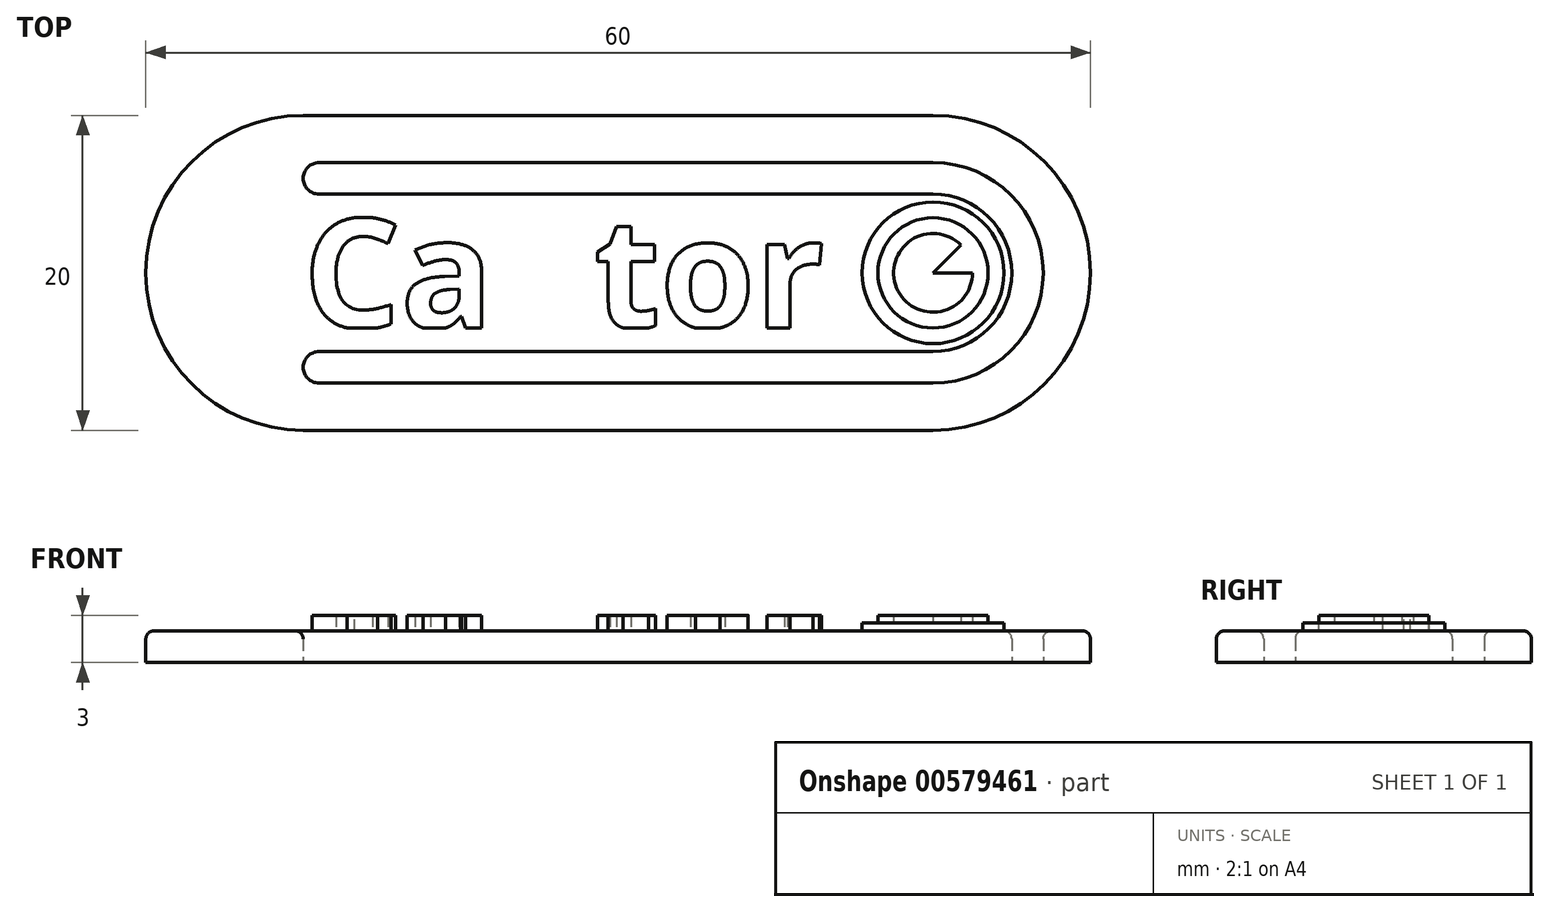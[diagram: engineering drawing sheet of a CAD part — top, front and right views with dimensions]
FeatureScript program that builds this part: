
annotation { "Feature Type Name" : "Feature", "Feature Type Description" : "" }
export const myFeature = defineFeature(function(context is Context, id is Id, definition is map)
    precondition{}
    {
        {
            var Q0;
            Q0=qCreatedBy(makeId("Top.planeOp"),FACE);
            var sketch = newSketch(context, id + "F0", { "sketchPlane" : qUnion([Q0])});
            skLineSegment(sketch, "E0.bottom", {"start": v(10, 0) * mm, "end": v(50, 0) * mm});
            skLineSegment(sketch, "E0.top", {"start": v(10, 20) * mm, "end": v(50, 20) * mm});
            skLineSegment(sketch, "E0.left", {"start": v(0, 10) * mm, "end": v(0, 10) * mm});
            skLineSegment(sketch, "E0.right", {"start": v(60, 10) * mm, "end": v(60, 10) * mm});
            skPoint(sketch, "E1.visualSharp", {"position": v(0, 0) * mm});
            skArc(sketch, "E1.filletArc", {"start": v(0, 10) * mm, "mid": v(2.93, 2.93) * mm, "end": v(10, 0) * mm});
            skPoint(sketch, "E2.visualSharp", {"position": v(0, 20) * mm});
            skArc(sketch, "E2.filletArc", {"start": v(10, 20) * mm, "mid": v(2.93, 17.07) * mm, "end": v(0, 10) * mm});
            skPoint(sketch, "E3.visualSharp", {"position": v(60, 20) * mm});
            skArc(sketch, "E3.filletArc", {"start": v(60, 10) * mm, "mid": v(57.07, 17.07) * mm, "end": v(50, 20) * mm});
            skPoint(sketch, "E4.visualSharp", {"position": v(60, 0) * mm});
            skArc(sketch, "E4.filletArc", {"start": v(50, 0) * mm, "mid": v(57.07, 2.93) * mm, "end": v(60, 10) * mm});
            skLineSegment(sketch, "E5.0", {"start": v(11, 3) * mm, "end": v(50, 3) * mm});
            skArc(sketch, "E5.1", {"start": v(50, 3) * mm, "mid": v(54.95, 5.05) * mm, "end": v(57, 10) * mm});
            skArc(sketch, "E5.2", {"start": v(57, 10) * mm, "mid": v(54.95, 14.95) * mm, "end": v(50, 17) * mm});
            skLineSegment(sketch, "E5.3", {"start": v(11, 17) * mm, "end": v(50, 17) * mm});
            skLineSegment(sketch, "E6.0", {"start": v(11, 5) * mm, "end": v(50, 5) * mm});
            skArc(sketch, "E6.1", {"start": v(50, 5) * mm, "mid": v(53.54, 6.46) * mm, "end": v(55, 10) * mm});
            skArc(sketch, "E6.2", {"start": v(55, 10) * mm, "mid": v(53.54, 13.54) * mm, "end": v(50, 15) * mm});
            skLineSegment(sketch, "E6.3", {"start": v(11, 15) * mm, "end": v(50, 15) * mm});
            skLineSegment(sketch, "E7", {"start": v(10, 16) * mm, "end": v(10, 16) * mm});
            skLineSegment(sketch, "E8", {"start": v(10, 4) * mm, "end": v(10, 4) * mm});
            skLineSegment(sketch, "E9.bottom", {"start": v(-20.23, 39.05) * mm, "end": v(-8.15, 39.05) * mm});
            skLineSegment(sketch, "E9.top", {"start": v(-21.23, 29.78) * mm, "end": v(-8.15, 29.78) * mm});
            skLineSegment(sketch, "E9.left", {"start": v(-21.23, 38.05) * mm, "end": v(-21.23, 29.78) * mm});
            skLineSegment(sketch, "E9.right", {"start": v(-8.15, 39.05) * mm, "end": v(-8.15, 29.78) * mm});
            skPoint(sketch, "E10.visualSharp", {"position": v(-21.23, 39.05) * mm});
            skArc(sketch, "E10.filletArc", {"start": v(-20.23, 39.05) * mm, "mid": v(-20.94, 38.76) * mm, "end": v(-21.23, 38.05) * mm});
            skPoint(sketch, "E11.visualSharp", {"position": v(10, 3) * mm});
            skArc(sketch, "E11.filletArc", {"start": v(10, 4) * mm, "mid": v(10.3, 3.3) * mm, "end": v(11, 3) * mm});
            skPoint(sketch, "E12.visualSharp", {"position": v(10, 5) * mm});
            skArc(sketch, "E12.filletArc", {"start": v(11, 5) * mm, "mid": v(10.3, 4.7) * mm, "end": v(10, 4) * mm});
            skPoint(sketch, "E13.visualSharp", {"position": v(10, 15) * mm});
            skArc(sketch, "E13.filletArc", {"start": v(10, 16) * mm, "mid": v(10.3, 15.3) * mm, "end": v(11, 15) * mm});
            skPoint(sketch, "E14.visualSharp", {"position": v(10, 17) * mm});
            skArc(sketch, "E14.filletArc", {"start": v(11, 17) * mm, "mid": v(10.3, 16.7) * mm, "end": v(10, 16) * mm});
            skSolve(sketch);
        }
        {
            var Q0;
            Q0=makeQuery(id+"F0.imprint","IMPRINT",FACE,{"disambiguationData":[TD([[makeQuery(id+"F0.imprint","IMPRINT",EDGE,{"derivedFrom":sQuery(id+"F0.wireOp",EDGE,"E0.bottom")}),1.0]])]});
            extrude(context, id + "F1", {"entities" : qUnion([Q0]), "depth" : 2 * mm, "offsetDistance" : 25 * mm});
        }
        {
            var Q0;
            Q0=makeQuery(id+"F1.opExtrude","CAP_EDGE",EDGE,{"disambiguationData":[OSD([sQuery(id+"F0.wireOp",EDGE,"E1.filletArc"),sQuery(id+"F0.wireOp",EDGE,"E2.filletArc")])],"isStart":false});
            var Q1;
            Q1=makeQuery(id+"F1.opExtrude","CAP_EDGE",EDGE,{"disambiguationData":[OSD([sQuery(id+"F0.wireOp",EDGE,"E5.3")])],"isStart":false});
            fillet(context, id + "F2", {"entities" : qUnion([Q0, Q1]), "radius" : 0.5 * mm, "tangentPropagation" : true, "allowEdgeOverflow" : false});
        }
        {
            var Q0;
            Q0=makeQuery(id+"F1.opExtrude","CAP_FACE",FACE,{"disambiguationData":[OSD([sQuery(id+"F0.wireOp",EDGE,"E0.bottom"),sQuery(id+"F0.wireOp",EDGE,"E0.top"),sQuery(id+"F0.wireOp",EDGE,"E1.filletArc"),sQuery(id+"F0.wireOp",EDGE,"E2.filletArc"),sQuery(id+"F0.wireOp",EDGE,"E3.filletArc"),sQuery(id+"F0.wireOp",EDGE,"E4.filletArc"),sQuery(id+"F0.wireOp",EDGE,"E5.0"),sQuery(id+"F0.wireOp",EDGE,"E5.1"),sQuery(id+"F0.wireOp",EDGE,"E5.2"),sQuery(id+"F0.wireOp",EDGE,"E5.3"),sQuery(id+"F0.wireOp",EDGE,"E6.0"),sQuery(id+"F0.wireOp",EDGE,"E6.1"),sQuery(id+"F0.wireOp",EDGE,"E6.2"),sQuery(id+"F0.wireOp",EDGE,"E6.3"),sQuery(id+"F0.wireOp",EDGE,"E11.filletArc"),sQuery(id+"F0.wireOp",EDGE,"E12.filletArc"),sQuery(id+"F0.wireOp",EDGE,"E13.filletArc"),sQuery(id+"F0.wireOp",EDGE,"E14.filletArc")])],"isStart":false});
            var sketch = newSketch(context, id + "F3", { "sketchPlane" : qUnion([Q0])});
            skLineSegment(sketch, "E15.0", {"start": v(10, 6.5) * mm, "end": v(50, 6.5) * mm});
            skArc(sketch, "E15.1", {"start": v(10, 13.5) * mm, "mid": v(6.5, 10) * mm, "end": v(10, 6.5) * mm});
            skLineSegment(sketch, "E15.2", {"start": v(50, 13.5) * mm, "end": v(10, 13.5) * mm});
            skArc(sketch, "E15.3", {"start": v(50, 6.5) * mm, "mid": v(53.5, 10) * mm, "end": v(50, 13.5) * mm});
            skText(sketch, "E16", { "text": "Cantor", "fontName": "OpenSans-Bold.ttf"});
            const initialGuessF3  = {"E16": [0.01, 0.0065, 1, 0, 0.007]};
            skSetInitialGuess(sketch, initialGuessF3);
            skSolve(sketch);
        }
        {
            var Q0;
            Q0=makeQuery(id+"F3.imprint","IMPRINT",FACE,{"disambiguationData":[TD([[makeQuery(id+"F3.imprint","IMPRINT",EDGE,{"derivedFrom":sQuery(id+"F3.wireOp",EDGE,"E16.sketch_text.stroke-0")}),-1.0]])]});
            var Q1;
            Q1=makeQuery(id+"F3.imprint","IMPRINT",FACE,{"disambiguationData":[TD([[makeQuery(id+"F3.imprint","IMPRINT",EDGE,{"derivedFrom":sQuery(id+"F3.wireOp",EDGE,"E16.sketch_text.stroke-15")}),-1.0]])]});
            var Q2;
            Q2=makeQuery(id+"F3.imprint","IMPRINT",FACE,{"disambiguationData":[TD([[makeQuery(id+"F3.imprint","IMPRINT",EDGE,{"derivedFrom":sQuery(id+"F3.wireOp",EDGE,"E16.sketch_text.stroke-40")}),-1.0]])]});
            var Q3;
            Q3=makeQuery(id+"F3.imprint","IMPRINT",FACE,{"disambiguationData":[TD([[makeQuery(id+"F3.imprint","IMPRINT",EDGE,{"derivedFrom":sQuery(id+"F3.wireOp",EDGE,"E16.sketch_text.stroke-75")}),-1.0]])]});
            var Q4;
            Q4=makeQuery(id+"F3.imprint","IMPRINT",FACE,{"disambiguationData":[TD([[makeQuery(id+"F3.imprint","IMPRINT",EDGE,{"derivedFrom":sQuery(id+"F3.wireOp",EDGE,"E16.sketch_text.stroke-57")}),-1.0]])]});
            var Q5;
            Q5=makeQuery(id+"F3.imprint","IMPRINT",FACE,{"disambiguationData":[TD([[makeQuery(id+"F3.imprint","IMPRINT",EDGE,{"derivedFrom":sQuery(id+"F3.wireOp",EDGE,"E16.sketch_text.stroke-93")}),-1.0]])]});
            extrude(context, id + "F4", {"entities" : qUnion([Q0, Q1, Q2, Q3, Q4, Q5]), "operationType" : NewBodyOperationType.ADD, "depth" : 1 * mm, "offsetDistance" : 25 * mm});
        }
        {
            var Q0;
            {var subQ5=sQuery(id+"F0.wireOp",EDGE,"E14.filletArc");var subQ6=sQuery(id+"F0.wireOp",EDGE,"E13.filletArc");var subQ7=sQuery(id+"F0.wireOp",EDGE,"E12.filletArc");var subQ8=sQuery(id+"F0.wireOp",EDGE,"E11.filletArc");var subQ9=sQuery(id+"F0.wireOp",EDGE,"E4.filletArc");var subQ10=sQuery(id+"F0.wireOp",EDGE,"E3.filletArc");var subQ11=sQuery(id+"F0.wireOp",EDGE,"E2.filletArc");var subQ12=sQuery(id+"F0.wireOp",EDGE,"E1.filletArc");var subQ13=sQuery(id+"F0.wireOp",EDGE,"E0.top");var subQ14=sQuery(id+"F0.wireOp",EDGE,"E0.bottom");var subQ17=sQuery(id+"F0.wireOp",EDGE,"E5.0");var subQ18=sQuery(id+"F0.wireOp",EDGE,"E5.2");var subQ19=sQuery(id+"F0.wireOp",EDGE,"E5.1");var subQ20=sQuery(id+"F0.wireOp",EDGE,"E5.3");var subQ23=sQuery(id+"F0.wireOp",EDGE,"E6.0");var subQ24=sQuery(id+"F0.wireOp",EDGE,"E6.2");var subQ25=sQuery(id+"F0.wireOp",EDGE,"E6.1");var subQ26=sQuery(id+"F0.wireOp",EDGE,"E6.3");Q0=makeQuery(id+"F4.boolean.opBoolean","SPLIT",FACE,{"disambiguationData":[TD([makeQuery(id+"F2.opFillet","BLEND_FACE",FACE,{"disambiguationData":[OSD([subQ14])]})])],"derivedFrom":makeQuery(id+"F1.opExtrude","CAP_FACE",FACE,{"disambiguationData":[OSD([subQ14,subQ13,subQ12,subQ11,subQ10,subQ9,subQ17,subQ19,subQ18,subQ20,subQ23,subQ25,subQ24,subQ26,subQ8,subQ7,subQ6,subQ5])],"isStart":false})});}
            var sketch = newSketch(context, id + "F5", { "sketchPlane" : qUnion([Q0])});
            skCircle(sketch, "E17", {"center": v(50, 10) * mm, "radius": 4.5 * mm});
            skPoint(sketch, "E17.first.point", {"position": v(50, 14.5) * mm});
            skPoint(sketch, "E17.second.point", {"position": v(50, 5.5) * mm});
            skPoint(sketch, "E17.third.point", {"position": v(54.5, 10) * mm});
            skSolve(sketch);
        }
        {
            var Q0;
            {var subQ0=sQuery(id+"F5.wireOp",EDGE,"E17");var subQ1=sQuery(id+"F0.wireOp",EDGE,"E6.3");var subQ2=sQuery(id+"F0.wireOp",EDGE,"E6.0");var subQ3=makeQuery(id+"F1.opExtrude","CAP_FACE",FACE,{"disambiguationData":[OSD([sQuery(id+"F0.wireOp",EDGE,"E0.bottom"),sQuery(id+"F0.wireOp",EDGE,"E0.top"),sQuery(id+"F0.wireOp",EDGE,"E1.filletArc"),sQuery(id+"F0.wireOp",EDGE,"E2.filletArc"),sQuery(id+"F0.wireOp",EDGE,"E3.filletArc"),sQuery(id+"F0.wireOp",EDGE,"E4.filletArc"),sQuery(id+"F0.wireOp",EDGE,"E5.0"),sQuery(id+"F0.wireOp",EDGE,"E5.1"),sQuery(id+"F0.wireOp",EDGE,"E5.2"),sQuery(id+"F0.wireOp",EDGE,"E5.3"),subQ2,sQuery(id+"F0.wireOp",EDGE,"E6.1"),sQuery(id+"F0.wireOp",EDGE,"E6.2"),subQ1,sQuery(id+"F0.wireOp",EDGE,"E11.filletArc"),sQuery(id+"F0.wireOp",EDGE,"E12.filletArc"),sQuery(id+"F0.wireOp",EDGE,"E13.filletArc"),sQuery(id+"F0.wireOp",EDGE,"E14.filletArc")])],"isStart":false});var subQ4=makeQuery(id+"F5.imprint","INTERSECT",VERTEX,{"derivedFrom":[makeQuery(id+"F2.opFillet","BLEND_EDGE",EDGE,{"blendedFrom":[makeQuery(id+"F1.opExtrude","CAP_EDGE",EDGE,{"disambiguationData":[OSD([subQ2])],"isStart":false}),subQ3],"blendedInto":[subQ3]}),subQ0]});Q0=makeQuery(id+"F5.imprint","IMPRINT",FACE,{"disambiguationData":[TD([[makeQuery(id+"F5.imprint","IMPRINT",EDGE,{"disambiguationData":[TD([[subQ4,1.0]])],"derivedFrom":subQ0}),1.0]])]});}
            extrude(context, id + "F6", {"entities" : qUnion([Q0]), "operationType" : NewBodyOperationType.ADD, "depth" : 0.5 * mm, "offsetDistance" : 25 * mm});
        }
        {
            var Q0;
            Q0=makeQuery(id+"F6.opExtrude","CAP_FACE",FACE,{"disambiguationData":[OSD([sQuery(id+"F5.wireOp",EDGE,"E17")])],"isStart":false});
            var sketch = newSketch(context, id + "F7", { "sketchPlane" : qUnion([Q0])});
            skCircle(sketch, "E18.0", {"center": v(50, 10) * mm, "radius": 3.5 * mm});
            skCircle(sketch, "E19.0", {"center": v(50, 10) * mm, "radius": 2.5 * mm});
            skLineSegment(sketch, "E20", {"start": v(50, 10) * mm, "end": v(53.5, 10) * mm});
            skLineSegment(sketch, "E21", {"start": v(53.5, 10) * mm, "end": v(50, 10) * mm});
            skLineSegment(sketch, "E22", {"start": v(50, 10) * mm, "end": v(52.47, 12.47) * mm});
            skLineSegment(sketch, "E23", {"start": v(50, 10) * mm, "end": v(50, 13.5) * mm});
            skSolve(sketch);
        }
        {
            var Q0;
            {var subQ0=sQuery(id+"F7.wireOp",EDGE,"E21");var subQ1=sQuery(id+"F7.wireOp",EDGE,"E18.0");var subQ2=makeQuery(id+"F7.imprint","INTERSECT",VERTEX,{"derivedFrom":[subQ1,subQ0]});Q0=makeQuery(id+"F7.imprint","IMPRINT",FACE,{"disambiguationData":[TD([[makeQuery(id+"F7.imprint","IMPRINT",EDGE,{"disambiguationData":[TD([[subQ2,1.0]])],"derivedFrom":subQ1}),1.0]])]});}
            var Q1;
            {var subQ0=sQuery(id+"F7.wireOp",EDGE,"E22");var subQ1=sQuery(id+"F7.wireOp",EDGE,"E19.0");var subQ2=makeQuery(id+"F7.imprint","INTERSECT",VERTEX,{"derivedFrom":[subQ1,subQ0]});Q1=makeQuery(id+"F7.imprint","IMPRINT",FACE,{"disambiguationData":[TD([[makeQuery(id+"F7.imprint","IMPRINT",EDGE,{"disambiguationData":[TD([[subQ2,1.0]])],"derivedFrom":subQ1}),1.0]])]});}
            var Q2;
            {var subQ0=sQuery(id+"F7.wireOp",EDGE,"E21");var subQ1=sQuery(id+"F7.wireOp",EDGE,"E18.0");var subQ2=makeQuery(id+"F7.imprint","INTERSECT",VERTEX,{"derivedFrom":[subQ1,subQ0]});Q2=makeQuery(id+"F7.imprint","IMPRINT",FACE,{"disambiguationData":[TD([[makeQuery(id+"F7.imprint","IMPRINT",EDGE,{"disambiguationData":[TD([[subQ2,-1.0]])],"derivedFrom":subQ1}),1.0]])]});}
            extrude(context, id + "F8", {"entities" : qUnion([Q0, Q1, Q2]), "operationType" : NewBodyOperationType.ADD, "depth" : 0.5 * mm, "offsetDistance" : 25 * mm});
        }
    });
